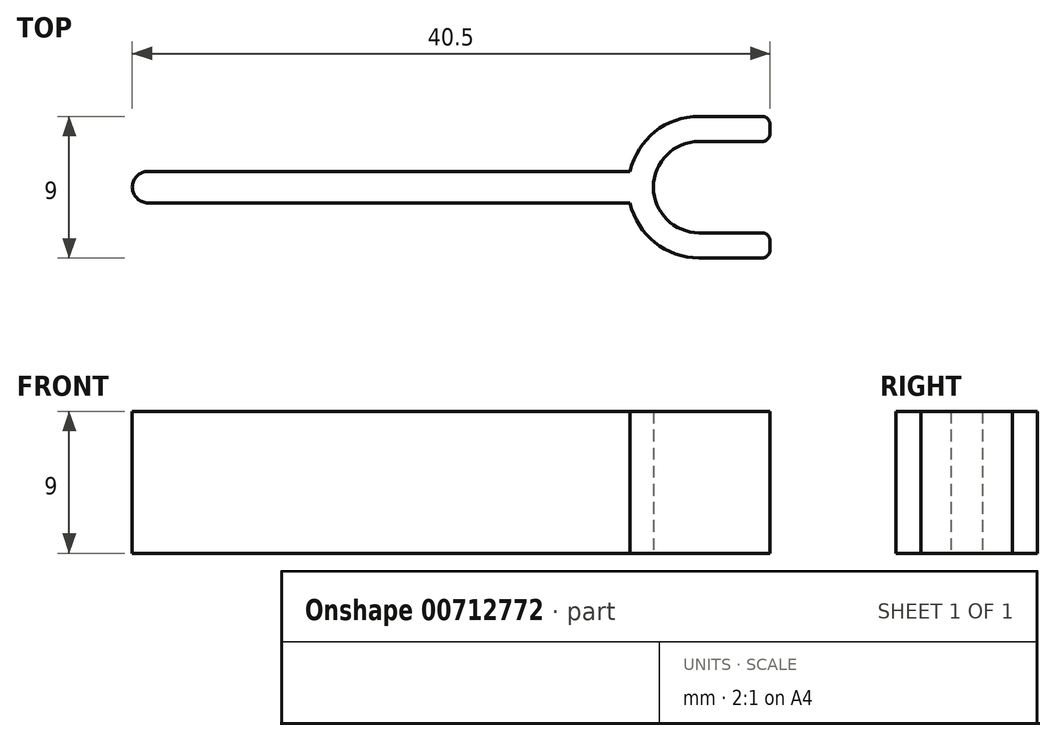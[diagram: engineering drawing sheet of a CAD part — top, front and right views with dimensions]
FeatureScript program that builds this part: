
annotation { "Feature Type Name" : "Feature", "Feature Type Description" : "" }
export const myFeature = defineFeature(function(context is Context, id is Id, definition is map)
    precondition{}
    {
        {
            var Q0;
            Q0=qCreatedBy(makeId("Top.planeOp"),FACE);
            var sketch = newSketch(context, id + "F0", { "sketchPlane" : qUnion([Q0])});
            skArc(sketch, "E0", {"start": v(0, 2.9) * mm, "mid": v(-2.9, 0) * mm, "end": v(0, -2.9) * mm});
            skArc(sketch, "E1", {"start": v(0, 4.5) * mm, "mid": v(-2.8, 3.52) * mm, "end": v(-4.39, 1) * mm});
            skLineSegment(sketch, "E2", {"start": v(0, 2.9) * mm, "end": v(4, 2.9) * mm});
            skLineSegment(sketch, "E3", {"start": v(0, 4.5) * mm, "end": v(4, 4.5) * mm});
            skLineSegment(sketch, "E4", {"start": v(0, -2.9) * mm, "end": v(4, -2.9) * mm});
            skLineSegment(sketch, "E5", {"start": v(0, -4.5) * mm, "end": v(4, -4.5) * mm});
            skLineSegment(sketch, "E6", {"start": v(4.5, 4) * mm, "end": v(4.5, 3.4) * mm});
            skLineSegment(sketch, "E7.trimOffspring", {"start": v(4.5, -3.4) * mm, "end": v(4.5, -4) * mm});
            skLineSegment(sketch, "E8", {"start": v(0, 0) * mm, "end": v(-35, 0) * mm, "construction": true});
            skPoint(sketch, "E8.endSnap0", {"position": v(-4.5, 0) * mm});
            skArc(sketch, "E9", {"start": v(-35, 1) * mm, "mid": v(-36, 0) * mm, "end": v(-35, -1) * mm});
            skLineSegment(sketch, "E10", {"start": v(-35, 1) * mm, "end": v(-4.39, 1) * mm});
            skLineSegment(sketch, "E11", {"start": v(-35, -1) * mm, "end": v(-4.39, -1) * mm});
            skArc(sketch, "E12.trimOffspring", {"start": v(-4.39, -1) * mm, "mid": v(-2.8, -3.52) * mm, "end": v(0, -4.5) * mm});
            skPoint(sketch, "E13.visualSharp", {"position": v(4.5, 4.5) * mm});
            skArc(sketch, "E13.filletArc", {"start": v(4.5, 4) * mm, "mid": v(4.35, 4.35) * mm, "end": v(4, 4.5) * mm});
            skPoint(sketch, "E14.visualSharp", {"position": v(4.5, 2.9) * mm});
            skArc(sketch, "E14.filletArc", {"start": v(4, 2.9) * mm, "mid": v(4.35, 3.05) * mm, "end": v(4.5, 3.4) * mm});
            skPoint(sketch, "E15.visualSharp", {"position": v(4.5, -2.9) * mm});
            skArc(sketch, "E15.filletArc", {"start": v(4.5, -3.4) * mm, "mid": v(4.35, -3.05) * mm, "end": v(4, -2.9) * mm});
            skPoint(sketch, "E16.visualSharp", {"position": v(4.5, -4.5) * mm});
            skArc(sketch, "E16.filletArc", {"start": v(4, -4.5) * mm, "mid": v(4.35, -4.35) * mm, "end": v(4.5, -4) * mm});
            skSolve(sketch);
        }
        {
            var Q0;
            Q0=makeQuery(id+"F0.imprint","IMPRINT",FACE,{"disambiguationData":[TD([[makeQuery(id+"F0.imprint","IMPRINT",EDGE,{"derivedFrom":sQuery(id+"F0.wireOp",EDGE,"E0")}),-1.0]])]});
            extrude(context, id + "F1", {"entities" : qUnion([Q0]), "depth" : 9 * mm, "offsetDistance" : 25 * mm});
        }
    });
